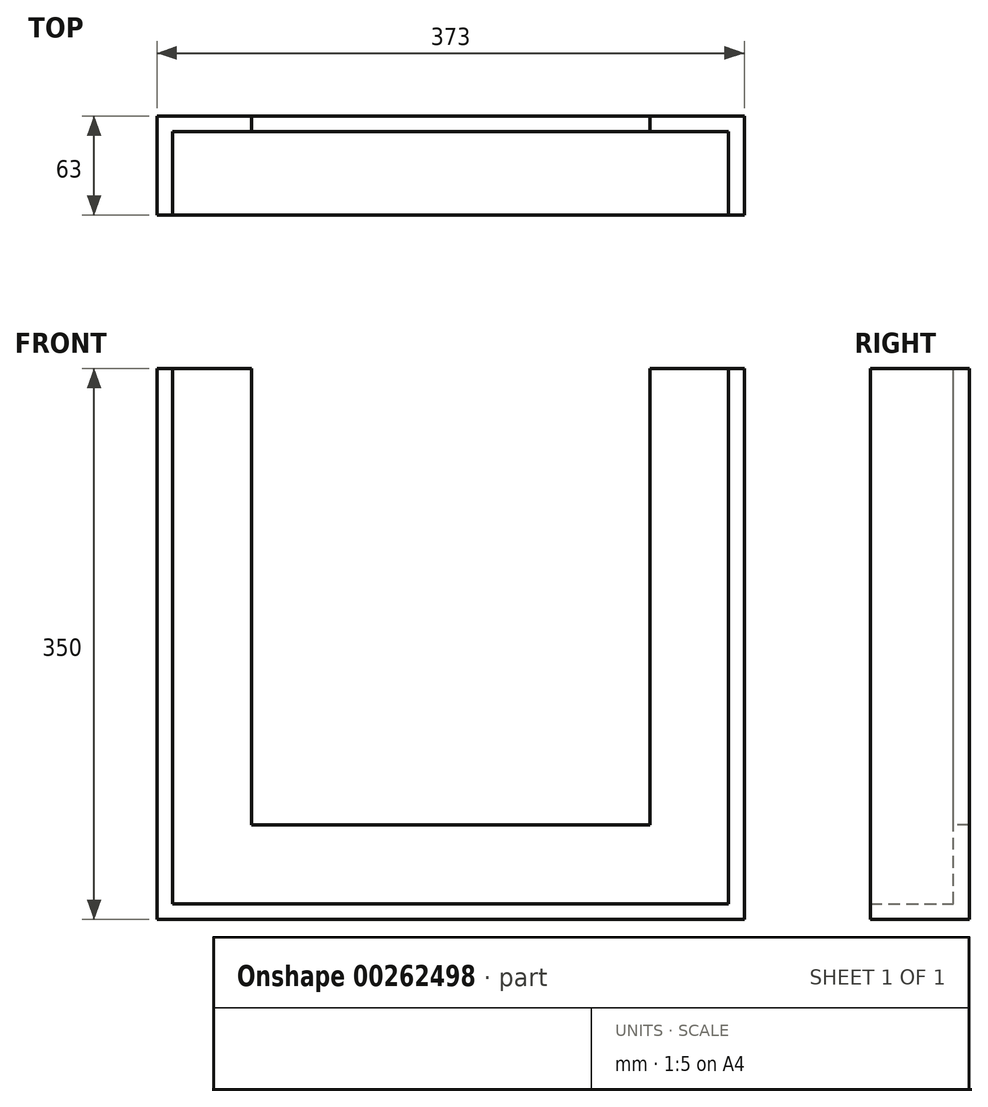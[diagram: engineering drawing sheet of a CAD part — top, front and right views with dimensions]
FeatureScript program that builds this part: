
annotation { "Feature Type Name" : "Feature", "Feature Type Description" : "" }
export const myFeature = defineFeature(function(context is Context, id is Id, definition is map)
    precondition{}
    {
        {
            var Q0;
            Q0=qCreatedBy(makeId("Front.planeOp"),FACE);
            var sketch = newSketch(context, id + "F0", { "sketchPlane" : qUnion([Q0])});
            skLineSegment(sketch, "E0.bottom", {"start": v(0, 0) * mm, "end": v(353, 0) * mm});
            skLineSegment(sketch, "E0.top", {"start": v(0, 10) * mm, "end": v(353, 10) * mm});
            skLineSegment(sketch, "E0.left", {"start": v(0, 0) * mm, "end": v(0, 10) * mm});
            skLineSegment(sketch, "E0.right", {"start": v(353, 0) * mm, "end": v(353, 10) * mm});
            skSolve(sketch);
        }
        {
            var Q0;
            Q0 = qSketchRegion(id + "F0", true);
            extrude(context, id + "F1", {"entities" : qUnion([Q0]), "depth" : 53 * mm});
        }
        {
            var Q0;
            Q0=makeQuery(id+"F1.opExtrude","CAP_FACE",FACE,{"disambiguationData":[OSD([sQuery(id+"F0.wireOp",EDGE,"E0.bottom"),sQuery(id+"F0.wireOp",EDGE,"E0.top"),sQuery(id+"F0.wireOp",EDGE,"E0.left"),sQuery(id+"F0.wireOp",EDGE,"E0.right")])],"isStart":false});
            var sketch = newSketch(context, id + "F2", { "sketchPlane" : qUnion([Q0])});
            skLineSegment(sketch, "E1.bottom", {"start": v(353, 0) * mm, "end": v(363, 0) * mm});
            skLineSegment(sketch, "E1.top", {"start": v(353, 350) * mm, "end": v(363, 350) * mm});
            skLineSegment(sketch, "E1.left", {"start": v(353, 0) * mm, "end": v(353, 350) * mm});
            skLineSegment(sketch, "E1.right", {"start": v(363, 0) * mm, "end": v(363, 350) * mm});
            skLineSegment(sketch, "E2.bottom", {"start": v(0, 0) * mm, "end": v(-10, 0) * mm});
            skLineSegment(sketch, "E2.top", {"start": v(0, 350) * mm, "end": v(-10, 350) * mm});
            skLineSegment(sketch, "E2.left", {"start": v(0, 0) * mm, "end": v(0, 350) * mm});
            skLineSegment(sketch, "E2.right", {"start": v(-10, 0) * mm, "end": v(-10, 350) * mm});
            skSolve(sketch);
        }
        {
            var Q0;
            Q0 = qSketchRegion(id + "F2", true);
            extrude(context, id + "F3", {"entities" : qUnion([Q0]), "operationType" : NewBodyOperationType.ADD, "oppositeDirection" : true, "depth" : 63 * mm});
        }
        {
            var Q0;
            Q0=makeQuery(id+"F1.opExtrude","CAP_FACE",FACE,{"disambiguationData":[OSD([sQuery(id+"F0.wireOp",EDGE,"E0.bottom"),sQuery(id+"F0.wireOp",EDGE,"E0.top"),sQuery(id+"F0.wireOp",EDGE,"E0.left"),sQuery(id+"F0.wireOp",EDGE,"E0.right")])],"isStart":true});
            var sketch = newSketch(context, id + "F4", { "sketchPlane" : qUnion([Q0])});
            skLineSegment(sketch, "E3", {"start": v(0, 0) * mm, "end": v(0, 350) * mm});
            skLineSegment(sketch, "E4", {"start": v(0, 350) * mm, "end": v(-50, 350) * mm});
            skLineSegment(sketch, "E5", {"start": v(-50, 350) * mm, "end": v(-50, 60) * mm});
            skLineSegment(sketch, "E6", {"start": v(-50, 60) * mm, "end": v(-303, 60) * mm});
            skLineSegment(sketch, "E7", {"start": v(-303, 60) * mm, "end": v(-303, 350) * mm});
            skLineSegment(sketch, "E8", {"start": v(-303, 350) * mm, "end": v(-353, 350) * mm});
            skLineSegment(sketch, "E9", {"start": v(-353, 350) * mm, "end": v(-353, 0) * mm});
            skLineSegment(sketch, "E10", {"start": v(-353, 0) * mm, "end": v(0, 0) * mm});
            skSolve(sketch);
        }
        {
            var Q0;
            Q0 = qSketchRegion(id + "F4", true);
            extrude(context, id + "F5", {"entities" : qUnion([Q0]), "operationType" : NewBodyOperationType.ADD, "depth" : 10 * mm});
        }
    });
